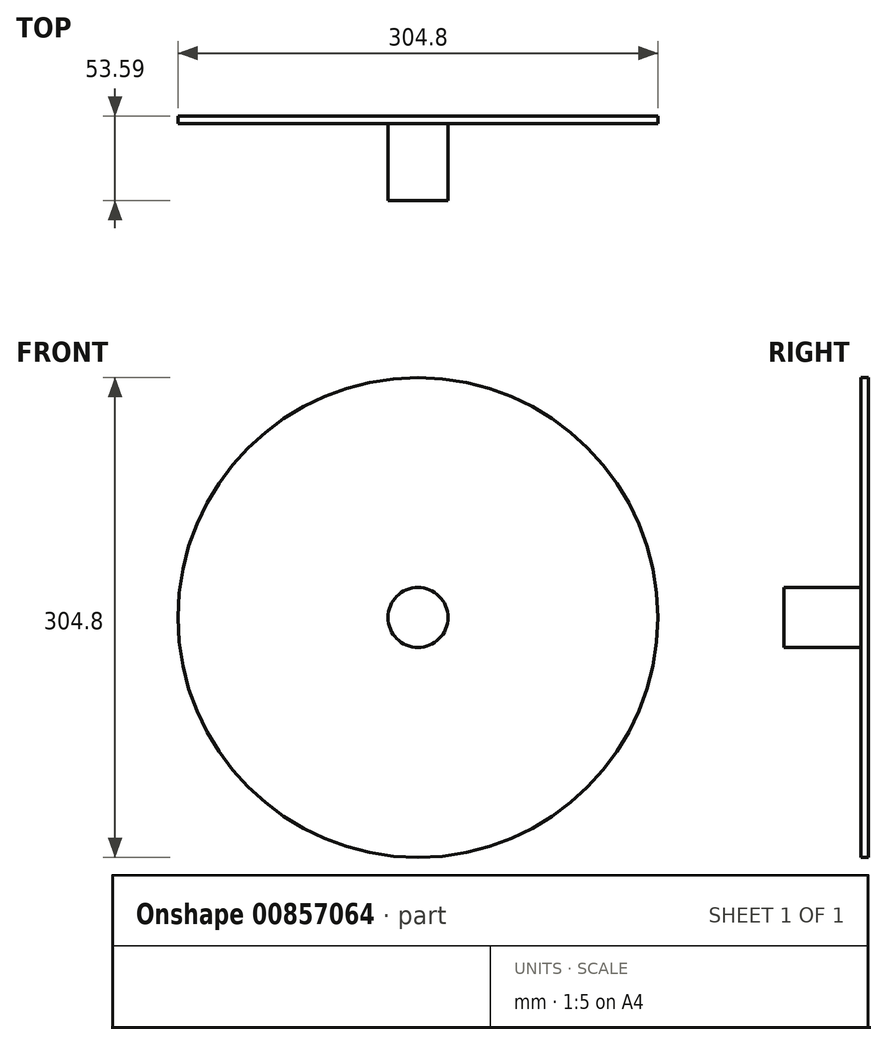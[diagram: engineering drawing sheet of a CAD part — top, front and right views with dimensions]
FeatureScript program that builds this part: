
annotation { "Feature Type Name" : "Feature", "Feature Type Description" : "" }
export const myFeature = defineFeature(function(context is Context, id is Id, definition is map)
    precondition{}
    {
        {
            var Q0;
            Q0=qCreatedBy(makeId("Front.planeOp"),FACE);
            var sketch = newSketch(context, id + "F0", { "sketchPlane" : qUnion([Q0])});
            skCircle(sketch, "E0", {"center": v(0, 0) * mm, "radius": 152.4 * mm});
            skCircle(sketch, "E1", {"center": v(0, 0) * mm, "radius": 19.05 * mm});
            skLineSegment(sketch, "E2.bottom", {"start": v(-228.6, -177.8) * mm, "end": v(228.6, -177.8) * mm});
            skLineSegment(sketch, "E2.top", {"start": v(-228.6, 177.8) * mm, "end": v(228.6, 177.8) * mm});
            skLineSegment(sketch, "E2.left", {"start": v(-228.6, -177.8) * mm, "end": v(-228.6, 177.8) * mm});
            skLineSegment(sketch, "E2.right", {"start": v(228.6, -177.8) * mm, "end": v(228.6, 177.8) * mm});
            skSolve(sketch);
        }
        {
            var Q0;
            Q0=makeQuery(id+"F0.imprint","IMPRINT",FACE,{"disambiguationData":[TD([[makeQuery(id+"F0.imprint","IMPRINT",EDGE,{"derivedFrom":sQuery(id+"F0.wireOp",EDGE,"E1")}),1.0]])]});
            extrude(context, id + "F1", {"entities" : qUnion([Q0]), "depth" : 53.6 * mm, "offsetDistance" : 25.4 * mm});
        }
        {
            var Q0;
            Q0=makeQuery(id+"F0.imprint","IMPRINT",FACE,{"disambiguationData":[TD([[makeQuery(id+"F0.imprint","IMPRINT",EDGE,{"derivedFrom":sQuery(id+"F0.wireOp",EDGE,"E0")}),1.0]])]});
            extrude(context, id + "F2", {"entities" : qUnion([Q0]), "operationType" : NewBodyOperationType.ADD, "depth" : 4.76 * mm, "offsetDistance" : 25.4 * mm});
        }
        {
            var Q0;
            Q0=makeQuery(id+"F0.imprint","IMPRINT",FACE,{"disambiguationData":[TD([[makeQuery(id+"F0.imprint","IMPRINT",EDGE,{"derivedFrom":sQuery(id+"F0.wireOp",EDGE,"E0")}),-1.0]])]});
            extrude(context, id + "F3", {"entities" : qUnion([Q0]), "depth" : 15.88 * mm, "offsetDistance" : 25.4 * mm});
        }
        {
            var Q0;
            Q0=makeQuery(id+"F3.opExtrude","SWEPT_BODY",BODY,{"disambiguationData":[OSD([sQuery(id+"F0.wireOp",EDGE,"E0"),sQuery(id+"F0.wireOp",EDGE,"E2.bottom"),sQuery(id+"F0.wireOp",EDGE,"E2.top"),sQuery(id+"F0.wireOp",EDGE,"E2.left"),sQuery(id+"F0.wireOp",EDGE,"E2.right")])]});
            deleteBodies(context, id + "F4", {"entities" : qUnion([Q0])});
        }
    });
